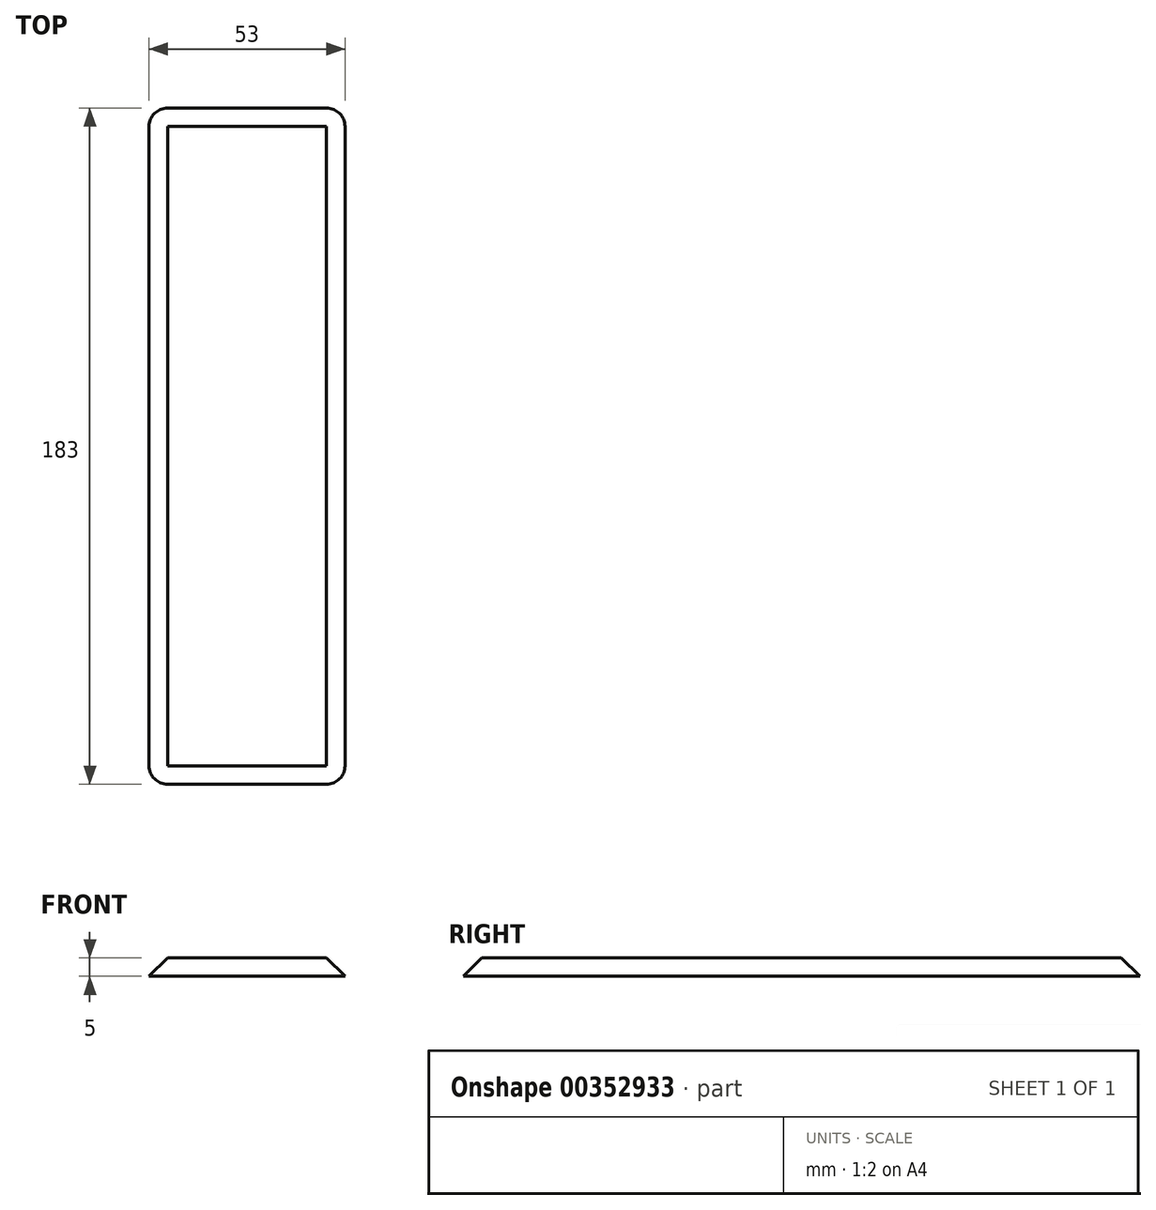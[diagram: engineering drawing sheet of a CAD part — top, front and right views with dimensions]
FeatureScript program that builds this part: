
annotation { "Feature Type Name" : "Feature", "Feature Type Description" : "" }
export const myFeature = defineFeature(function(context is Context, id is Id, definition is map)
    precondition{}
    {
        {
            var Q0;
            Q0=qCreatedBy(makeId("Top.planeOp"),FACE);
            var sketch = newSketch(context, id + "F0", { "sketchPlane" : qUnion([Q0])});
            skLineSegment(sketch, "E0.bottom", {"start": v(0, 0) * mm, "end": v(53, 0) * mm});
            skLineSegment(sketch, "E0.top", {"start": v(0, -183) * mm, "end": v(53, -183) * mm});
            skLineSegment(sketch, "E0.left", {"start": v(0, 0) * mm, "end": v(0, -183) * mm});
            skLineSegment(sketch, "E0.right", {"start": v(53, 0) * mm, "end": v(53, -183) * mm});
            skSolve(sketch);
        }
        {
            var Q0;
            Q0 = qSketchRegion(id + "F0", true);
            extrude(context, id + "F1", {"entities" : qUnion([Q0]), "depth" : 5 * mm, "offsetDistance" : 25 * mm});
        }
        {
            var Q0;
            Q0=makeQuery(id+"F1.opExtrude","SWEPT_EDGE",EDGE,{"disambiguationData":[OSD([sQuery(id+"F0.wireOp",EDGE,"E0.top"),sQuery(id+"F0.wireOp",EDGE,"E0.left")])]});
            var Q1;
            Q1=makeQuery(id+"F1.opExtrude","SWEPT_EDGE",EDGE,{"disambiguationData":[OSD([sQuery(id+"F0.wireOp",EDGE,"E0.top"),sQuery(id+"F0.wireOp",EDGE,"E0.right")])]});
            var Q2;
            Q2=makeQuery(id+"F1.opExtrude","SWEPT_EDGE",EDGE,{"disambiguationData":[OSD([sQuery(id+"F0.wireOp",EDGE,"E0.bottom"),sQuery(id+"F0.wireOp",EDGE,"E0.right")])]});
            var Q3;
            Q3=makeQuery(id+"F1.opExtrude","SWEPT_EDGE",EDGE,{"disambiguationData":[OSD([sQuery(id+"F0.wireOp",EDGE,"E0.bottom"),sQuery(id+"F0.wireOp",EDGE,"E0.left")])]});
            fillet(context, id + "F2", {"entities" : qUnion([Q0, Q1, Q2, Q3]), "tangentPropagation" : true, "radius" : 5 * mm, "defaultsChanged" : false, "vertexSettings" : [], "allowEdgeOverflow" : false});
        }
        {
            var Q0;
            Q0=makeQuery(id+"F1.opExtrude","CAP_EDGE",EDGE,{"disambiguationData":[OSD([sQuery(id+"F0.wireOp",EDGE,"E0.left")])],"isStart":false});
            chamfer(context, id + "F3", {"entities" : qUnion([Q0]), "width" : 5 * mm, "tangentPropagation" : true});
        }
    });
